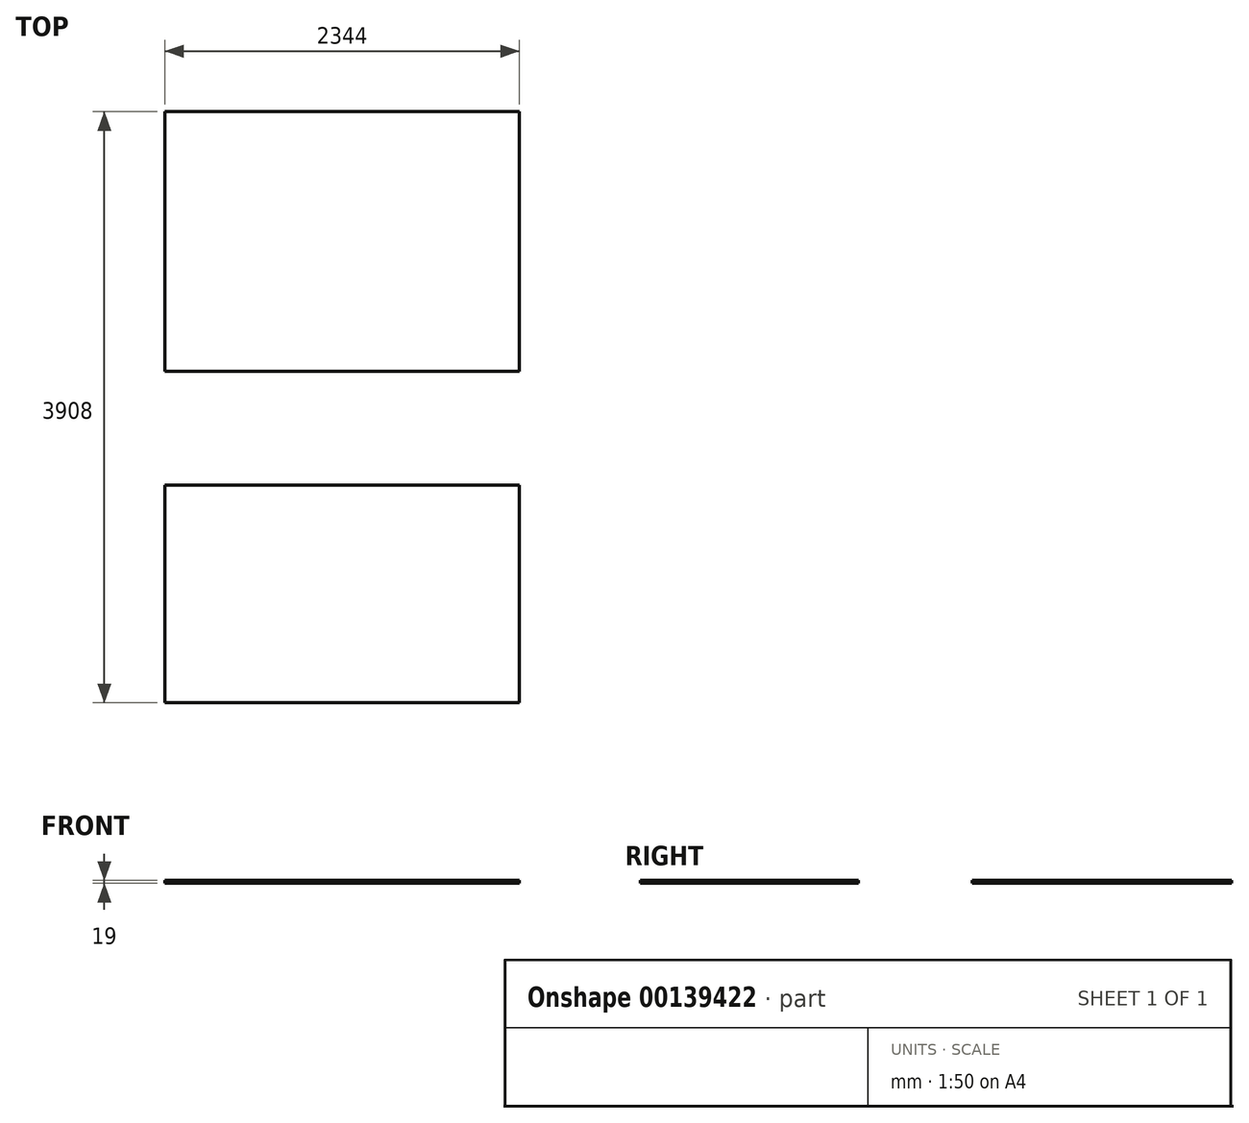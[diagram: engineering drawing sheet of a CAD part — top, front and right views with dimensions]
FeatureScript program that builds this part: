
annotation { "Feature Type Name" : "Feature", "Feature Type Description" : "" }
export const myFeature = defineFeature(function(context is Context, id is Id, definition is map)
    precondition{}
    {
        {
            var Q0;
            Q0=qCreatedBy(makeId("Top.planeOp"),FACE);
            var sketch = newSketch(context, id + "F0", { "sketchPlane" : qUnion([Q0])});
            skLineSegment(sketch, "E0.bottom", {"start": v(-1172, -422.33) * mm, "end": v(1172, -422.33) * mm});
            skLineSegment(sketch, "E0.top", {"start": v(-1172, -1862.33) * mm, "end": v(1172, -1862.33) * mm});
            skLineSegment(sketch, "E0.left", {"start": v(-1172, -422.33) * mm, "end": v(-1172, -1862.33) * mm});
            skLineSegment(sketch, "E0.right", {"start": v(1172, -422.33) * mm, "end": v(1172, -1862.33) * mm});
            skLineSegment(sketch, "E1.bottom", {"start": v(-852, -422.33) * mm, "end": v(852, -422.33) * mm});
            skLineSegment(sketch, "E1.top", {"start": v(-852, 330.67) * mm, "end": v(852, 330.67) * mm});
            skLineSegment(sketch, "E1.left", {"start": v(-852, -422.33) * mm, "end": v(-852, 330.67) * mm});
            skLineSegment(sketch, "E1.right", {"start": v(852, -422.33) * mm, "end": v(852, 330.67) * mm});
            skLineSegment(sketch, "E2.bottom", {"start": v(-1172, 330.67) * mm, "end": v(1172, 330.67) * mm});
            skLineSegment(sketch, "E2.top", {"start": v(-1172, 2045.67) * mm, "end": v(1172, 2045.67) * mm});
            skLineSegment(sketch, "E2.left", {"start": v(-1172, 330.67) * mm, "end": v(-1172, 2045.67) * mm});
            skLineSegment(sketch, "E2.right", {"start": v(1172, 330.67) * mm, "end": v(1172, 2045.67) * mm});
            skSolve(sketch);
        }
        {
            var Q0;
            Q0=makeQuery(id+"F0.imprint","IMPRINT",FACE,{"disambiguationData":[TD([[makeQuery(id+"F0.imprint","IMPRINT",EDGE,{"derivedFrom":sQuery(id+"F0.wireOp",EDGE,"E2.top")}),-1.0]])]});
            var Q1;
            Q1=makeQuery(id+"F0.imprint","IMPRINT",FACE,{"disambiguationData":[TD([[makeQuery(id+"F0.imprint","IMPRINT",EDGE,{"derivedFrom":sQuery(id+"F0.wireOp",EDGE,"E1.bottom")}),1.0]])]});
            var Q2;
            Q2=makeQuery(id+"F0.imprint","IMPRINT",FACE,{"disambiguationData":[TD([[makeQuery(id+"F0.imprint","IMPRINT",EDGE,{"derivedFrom":sQuery(id+"F0.wireOp",EDGE,"E0.top")}),1.0]])]});
            extrude(context, id + "F1", {"entities" : qUnion([Q0, Q1, Q2]), "depth" : 19 * mm});
        }
    });
